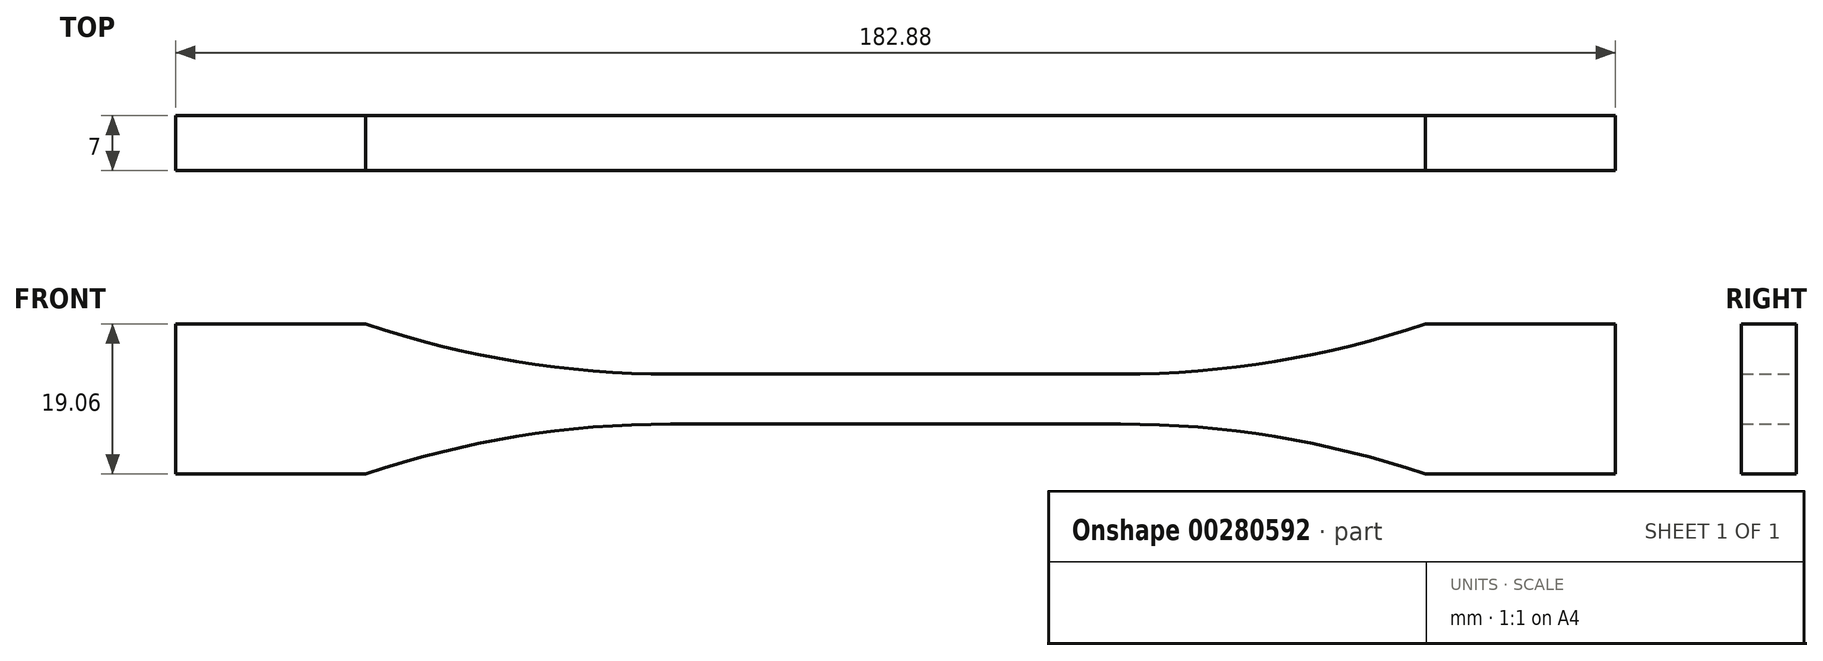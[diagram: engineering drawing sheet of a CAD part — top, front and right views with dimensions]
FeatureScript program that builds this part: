
annotation { "Feature Type Name" : "Feature", "Feature Type Description" : "" }
export const myFeature = defineFeature(function(context is Context, id is Id, definition is map)
    precondition{}
    {
        {
            var Q0;
            Q0=qCreatedBy(makeId("Front.planeOp"),FACE);
            var sketch = newSketch(context, id + "F0", { "sketchPlane" : qUnion([Q0])});
            skLineSegment(sketch, "E0", {"start": v(0, 3.18) * mm, "end": v(28.58, 3.18) * mm});
            skArc(sketch, "E1", {"start": v(28.58, 3.17) * mm, "mid": v(48.2, 4.77) * mm, "end": v(67.3, 9.52) * mm});
            skLineSegment(sketch, "E2", {"start": v(67.3, 9.52) * mm, "end": v(91.44, 9.52) * mm});
            skLineSegment(sketch, "E3", {"start": v(91.44, 9.52) * mm, "end": v(91.44, 0) * mm});
            skLineSegment(sketch, "E4.MirrorCS", {"start": v(0, -3.18) * mm, "end": v(28.58, -3.18) * mm});
            skLineSegment(sketch, "E5.MirrorCS", {"start": v(91.44, -9.52) * mm, "end": v(91.44, 0) * mm});
            skLineSegment(sketch, "E6.MirrorCS", {"start": v(67.3, -9.53) * mm, "end": v(91.44, -9.53) * mm});
            skArc(sketch, "E7.MirrorCS", {"start": v(28.58, -3.17) * mm, "mid": v(48.2, -4.77) * mm, "end": v(67.3, -9.52) * mm});
            skArc(sketch, "E8.MirrorCS", {"start": v(-28.58, 3.17) * mm, "mid": v(-48.2, 4.77) * mm, "end": v(-67.31, 9.52) * mm});
            skLineSegment(sketch, "E9.MirrorCS", {"start": v(-91.44, 9.52) * mm, "end": v(-91.44, 0) * mm});
            skArc(sketch, "E10.MirrorCS", {"start": v(-28.58, -3.17) * mm, "mid": v(-48.2, -4.77) * mm, "end": v(-67.3, -9.52) * mm});
            skLineSegment(sketch, "E11.MirrorCS", {"start": v(-67.3, -9.52) * mm, "end": v(-91.44, -9.52) * mm});
            skLineSegment(sketch, "E12.MirrorCS", {"start": v(-67.31, 9.52) * mm, "end": v(-91.44, 9.52) * mm});
            skLineSegment(sketch, "E13.MirrorCS", {"start": v(-91.44, -9.52) * mm, "end": v(-91.44, 0) * mm});
            skLineSegment(sketch, "E14.MirrorCS", {"start": v(0, -3.18) * mm, "end": v(-28.58, -3.18) * mm});
            skLineSegment(sketch, "E15.MirrorCS", {"start": v(0, 3.18) * mm, "end": v(-28.58, 3.18) * mm});
            skArc(sketch, "E16.MirrorCS", {"start": v(-28.58, 3.17) * mm, "mid": v(-48.2, 4.77) * mm, "end": v(-67.3, 9.52) * mm});
            skSolve(sketch);
        }
        {
            var Q0;
            Q0=makeQuery(id+"F0.imprint","IMPRINT",FACE,{"disambiguationData":[TD([[makeQuery(id+"F0.imprint","IMPRINT",EDGE,{"derivedFrom":sQuery(id+"F0.wireOp",EDGE,"E1")}),-1.0]])]});
            extrude(context, id + "F1", {"entities" : qUnion([Q0]), "endBound" : BoundingType.SYMMETRIC, "depth" : 7 * mm});
        }
    });
